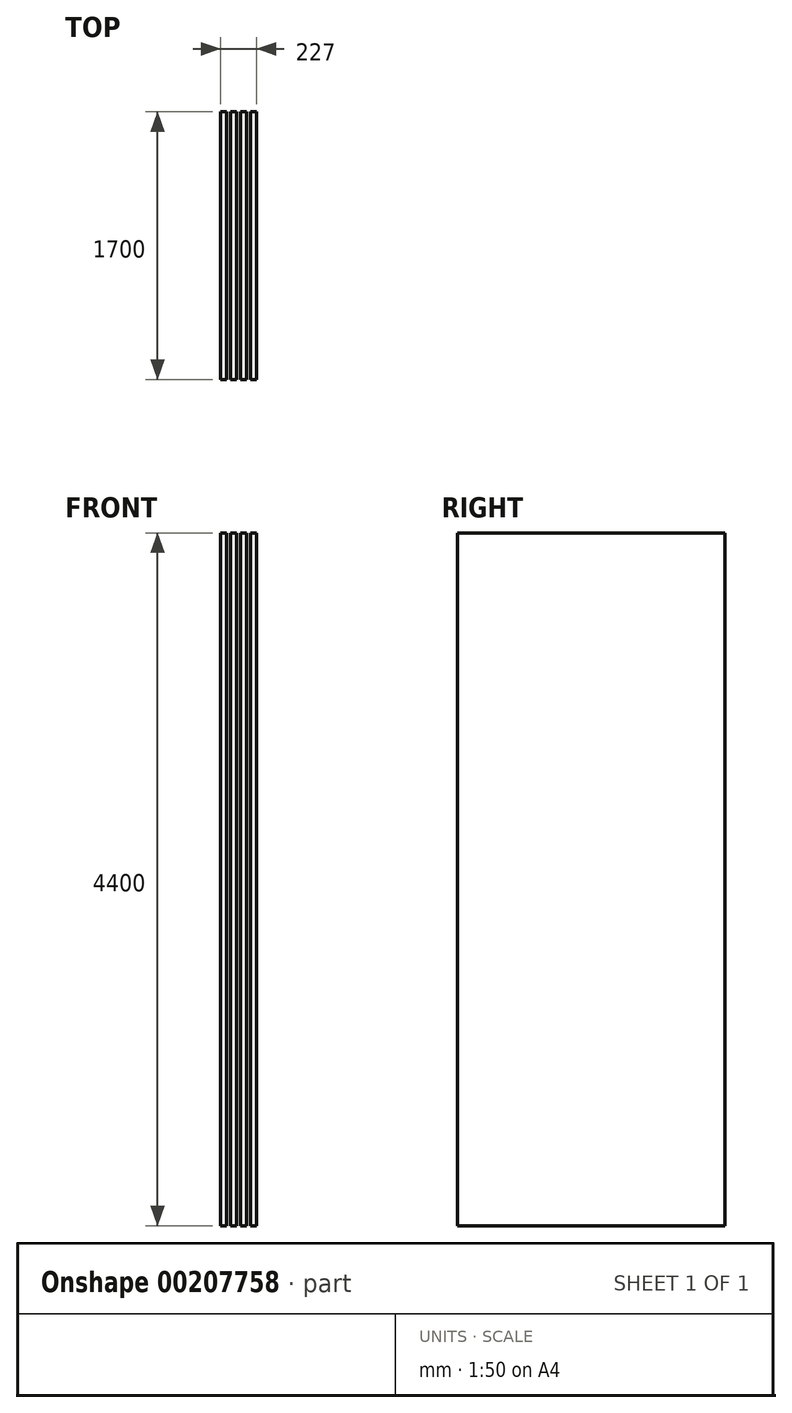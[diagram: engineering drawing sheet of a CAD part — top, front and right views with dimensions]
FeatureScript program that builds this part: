
annotation { "Feature Type Name" : "Feature", "Feature Type Description" : "" }
export const myFeature = defineFeature(function(context is Context, id is Id, definition is map)
    precondition{}
    {
        {
            var Q0;
            Q0=qCreatedBy(makeId("Front.planeOp"),FACE);
            var sketch = newSketch(context, id + "F0", { "sketchPlane" : qUnion([Q0])});
            skLineSegment(sketch, "E0.bottom", {"start": v(1900, 6661) * mm, "end": v(1938, 6661) * mm});
            skLineSegment(sketch, "E0.top", {"start": v(1900, 2261) * mm, "end": v(1938, 2261) * mm});
            skLineSegment(sketch, "E0.left", {"start": v(1900, 6661) * mm, "end": v(1900, 2261) * mm});
            skLineSegment(sketch, "E0.right", {"start": v(1938, 6661) * mm, "end": v(1938, 2261) * mm});
            skLineSegment(sketch, "E1.bottom", {"start": v(1963, 6661) * mm, "end": v(2001, 6661) * mm});
            skLineSegment(sketch, "E1.top", {"start": v(1963, 2261) * mm, "end": v(2001, 2261) * mm});
            skLineSegment(sketch, "E1.left", {"start": v(1963, 6661) * mm, "end": v(1963, 2261) * mm});
            skLineSegment(sketch, "E1.right", {"start": v(2001, 6661) * mm, "end": v(2001, 2261) * mm});
            skLineSegment(sketch, "E2.bottom", {"start": v(2026, 6661) * mm, "end": v(2064, 6661) * mm});
            skLineSegment(sketch, "E2.top", {"start": v(2026, 2261) * mm, "end": v(2064, 2261) * mm});
            skLineSegment(sketch, "E2.left", {"start": v(2026, 6661) * mm, "end": v(2026, 2261) * mm});
            skLineSegment(sketch, "E2.right", {"start": v(2064, 6661) * mm, "end": v(2064, 2261) * mm});
            skLineSegment(sketch, "E3.bottom", {"start": v(2089, 6661) * mm, "end": v(2127, 6661) * mm});
            skLineSegment(sketch, "E3.top", {"start": v(2089, 2261) * mm, "end": v(2127, 2261) * mm});
            skLineSegment(sketch, "E3.left", {"start": v(2089, 6661) * mm, "end": v(2089, 2261) * mm});
            skLineSegment(sketch, "E3.right", {"start": v(2127, 6661) * mm, "end": v(2127, 2261) * mm});
            skSolve(sketch);
        }
        {
            var Q0;
            Q0 = qSketchRegion(id + "F0", true);
            extrude(context, id + "F1", {"entities" : qUnion([Q0]), "endBound" : BoundingType.SYMMETRIC, "depth" : 1700 * mm, "offsetDistance" : 25 * mm});
        }
    });
